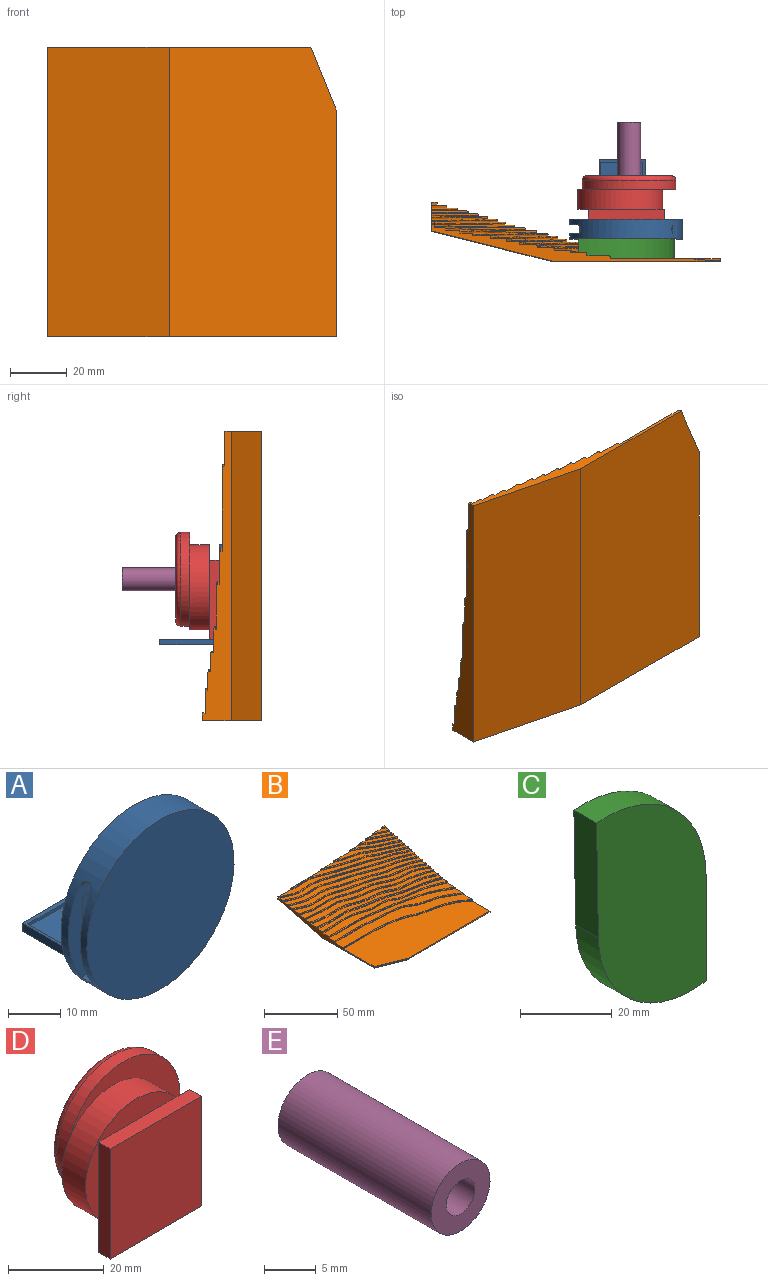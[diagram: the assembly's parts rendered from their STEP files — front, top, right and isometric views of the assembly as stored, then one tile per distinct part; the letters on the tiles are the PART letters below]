
ASSEMBLY  parts=5 mates=4
PART A: 31 faces, bbox 39.9x28x39.9 mm
  f0: plane 36.2x21.53mm, normal (0,-1,0), area 287.6mm2, adj f1,f14,f16,f17,f18,f19,f20,f21
  f1: cylinder r=19.96mm len=39.91mm, axis (0,-1,0), area 799mm2, adj f0,f3,f4,f14,f15,f16,f17
  f2: plane 21x16.52mm, normal (0,0,1), area 136.6mm2, adj f3,f5,f7,f8,f9,f10,f11,f12
  f3: plane 39.91x39.91mm, normal (0,1,0), area 1220mm2, adj f1,f2,f5,f6,f7
  f4: plane 39.91x39.91mm, normal (0,-1,0), area 1251mm2, adj f1
  f5: plane 21x1.88mm, normal (1,0,0), area 39.5mm2, adj f2,f3,f6,f8
  f6: plane 21x16.52mm, normal (0,0,-1), area 346.9mm2, adj f3,f5,f7,f8
  f7: plane 21x1.88mm, normal (-1,0,0), area 39.5mm2, adj f2,f3,f6,f8
  f8: plane 16.52x1.88mm, normal (0,1,0), area 31.1mm2, adj f2,f5,f6,f7
  f9: plane 14.58x0.7mm, normal (0,-1,0), area 10.2mm2, adj f2,f10,f12,f13
  f10: plane 14.42x0.7mm, normal (1,0,0), area 10.1mm2, adj f2,f9,f11,f13
  f11: plane 14.58x0.7mm, normal (0,1,0), area 10.2mm2, adj f2,f10,f12,f13
  f12: plane 14.42x0.7mm, normal (-1,0,0), area 10.1mm2, adj f2,f9,f11,f13
  f13: plane 14.58x14.42mm, normal (0,0,1), area 210.3mm2, adj f9,f10,f11,f12
  f14: cylinder r=1.62mm len=33.46mm, axis (1,0,0), area 166.7mm2, adj f0,f1,f15,f17
  f15: plane 36.2x21.53mm, normal (0,1,0), area 757.2mm2, adj f1,f14,f16,f17
  f16: plane 32.6x3.24mm, normal (0,0,1), area 105.5mm2, adj f0,f1,f15,f17
  f17: plane 23.02x3.24mm, normal (-1,0,0), area 73.7mm2, adj f0,f1,f14,f15,f16
  f18: plane 30.97x1.82mm, normal (0,0,-1), area 56.4mm2, adj f0,f19,f21,f22
  f19: plane 15.16x1.82mm, normal (1,0,0), area 27.6mm2, adj f0,f18,f20,f22
  f20: plane 30.97x1.82mm, normal (0,0,1), area 56.4mm2, adj f0,f19,f21,f22
  f21: plane 15.16x1.82mm, normal (-1,0,0), area 27.6mm2, adj f0,f18,f20,f22
  f22: plane 30.97x15.16mm, normal (0,-1,0), area 469.6mm2, adj f18,f19,f20,f21
  f23: cylinder r=17.46mm len=20.68mm, axis (0,-1,0), area 43.6mm2, adj f24,f25,f26
  f24: plane 20.68x3.39mm, normal (0,-1,0), area 47.7mm2, adj f23,f26
  f25: plane 20.56x3.35mm, normal (0,1,0), area 46.9mm2, adj f23,f26
  f26: cylinder r=4.12mm len=20.68mm, axis (1,0,0), area 41.2mm2, adj f23,f24,f25
  f27: plane 21.02x2mm, normal (0,0,-1), area 42mm2, adj f28,f29,f30
  f28: plane 21.02x3.52mm, normal (0,-1,0), area 50.4mm2, adj f27,f30
  f29: plane 21.02x3.52mm, normal (0,1,0), area 50.4mm2, adj f27,f30
  f30: cylinder r=17.46mm len=21.02mm, axis (0,-1,0), area 45.1mm2, adj f27,f28,f29
PART B: 75 faces, bbox 113.4x105.4x21.6 mm
  f0: plane 102.85x10.84mm, normal (0,1,0), area 515.5mm2, adj f1,f3,f29,f30,f31,f33,f34,f36
  f1: plane 93.19x13.13mm, normal (-1,0,0), area 217.1mm2, adj f0,f2,f5,f6,f7,f8,f9,f10
  f2: plane 102.21x59.09mm, normal (0,0,-1), area 5941.1mm2, adj f1,f3,f4,f48,f74
  f3: plane 102.21x21.2mm, normal (1,0,0), area 618.2mm2, adj f0,f2,f4,f5,f6,f7,f8,f9
  f4: plane 80.7x1.62mm, normal (0,-1,0), area 80mm2, adj f2,f3,f5,f48,f49
  f5: plane 102.21x39.62mm, normal (0,0,1), area 3289.8mm2, adj f1,f3,f4,f6,f49
  f6: extruded ~102.21x22.7mm, area 53.4mm2, adj f1,f3,f5,f72
  f7: plane 102.21x31.3mm, normal (0,0,1), area 884.1mm2, adj f1,f3,f8,f72
  f8: extruded ~102.21x21.85mm, area 53.2mm2, adj f1,f3,f7,f71
  f9: plane 102.21x26.47mm, normal (0,0,1), area 540.6mm2, adj f1,f3,f10,f71
  f10: extruded ~102.21x19.55mm, area 52.7mm2, adj f1,f3,f9,f70
  f11: plane 102.21x26.07mm, normal (0,0,1), area 497.7mm2, adj f1,f3,f12,f70
  f12: extruded ~102.21x18.81mm, area 52.7mm2, adj f1,f3,f11,f69
  f13: plane 102.21x22.91mm, normal (0,0,1), area 341.3mm2, adj f1,f3,f68,f69
  f14: plane 102.21x24.07mm, normal (0,0,1), area 313.2mm2, adj f1,f3,f66,f67
  f15: plane 102.21x25.31mm, normal (0,0,1), area 456.2mm2, adj f1,f3,f16,f17,f65
  f16: extruded ~29.65x1.56mm, area 14.9mm2, adj f1,f15,f17,f63
  f17: extruded ~72.56x19.99mm, area 37.9mm2, adj f3,f15,f16,f64
  f18: plane 102.21x26.36mm, normal (0,0,1), area 411.6mm2, adj f1,f3,f19,f63,f64
  f19: extruded ~102.21x23.57mm, area 53mm2, adj f1,f3,f18,f62
  f20: plane 102.21x29.38mm, normal (0,0,1), area 432.2mm2, adj f1,f3,f21,f62
  f21: extruded ~102.21x26.65mm, area 53.4mm2, adj f1,f3,f20,f61
  f22: plane 102.21x30.63mm, normal (0,0,1), area 382.6mm2, adj f1,f3,f23,f24,f61
  f23: extruded ~66.71x16.06mm, area 34.7mm2, adj f1,f22,f24,f60
  f24: extruded ~35.5x11.14mm, area 18.7mm2, adj f3,f22,f23,f73
  f25: plane 102.22x31.84mm, normal (0,0,1), area 409.8mm2, adj f1,f3,f26,f60,f73
  f26: extruded ~102.21x28.45mm, area 53.6mm2, adj f1,f3,f25,f59
  f27: plane 102.21x31.74mm, normal (0,0,1), area 331.8mm2, adj f1,f3,f28,f59
  f28: extruded ~102.21x28.42mm, area 53.5mm2, adj f1,f3,f27,f58
  f29: plane 102.21x29.28mm, normal (0,0,1), area 344.6mm2, adj f0,f1,f3,f30,f58
  f30: extruded ~90.49x26.05mm, area 47.6mm2, adj f0,f3,f29,f57
  f31: plane 89.45x25.54mm, normal (0,0,1), area 229.2mm2, adj f0,f3,f32,f33,f57
  f32: extruded ~17.29x7.32mm, area 9.4mm2, adj f3,f31,f33,f56
  f33: extruded ~43.55x15.97mm, area 23.3mm2, adj f0,f31,f32,f55
  f34: plane 59.47x22.74mm, normal (0,0,1), area 189.9mm2, adj f0,f3,f35,f36,f55,f56
  f35: extruded ~33.87x15.02mm, area 18.6mm2, adj f3,f34,f36,f53
  f36: extruded ~15.25x4.76mm, area 8mm2, adj f0,f34,f35,f54
  f37: plane 47.79x19.23mm, normal (0,0,1), area 148.4mm2, adj f0,f3,f38,f53,f54
  f38: extruded ~33.35x16.57mm, area 18.7mm2, adj f0,f3,f37,f52
  f39: plane 32.1x16.6mm, normal (0,0,1), area 91.9mm2, adj f0,f3,f40,f52
  f40: extruded ~24.46x12.88mm, area 13.9mm2, adj f0,f3,f39,f51
  f41: plane 23.6x12.33mm, normal (0,0,1), area 70.5mm2, adj f0,f3,f42,f51
  f42: extruded ~18.21x9.13mm, area 10.2mm2, adj f0,f3,f41,f50
  f43: plane 17.17x8.57mm, normal (0,0,1), area 45.2mm2, adj f0,f3,f44,f50
  f44: plane 11.3x5.41mm, normal (-0.43,-0.9,0), area 12.5mm2, adj f0,f3,f43,f45
  f45: plane 11.3x5.41mm, normal (0,0,1), area 27.8mm2, adj f0,f3,f44,f46
  f46: plane 2.76x2.02mm, normal (-0.59,-0.81,0), area 3.4mm2, adj f0,f3,f45,f47
  f47: plane 2.76x2.02mm, normal (0,0,1), area 2.8mm2, adj f0,f3,f46
  f48: plane 22.13x8.94mm, normal (-0.37,-0.93,0), area 11.9mm2, adj f1,f2,f4,f49
  f49: bspline ~26x10.89mm, area 20mm2, adj f1,f4,f5,f48
  f50: bspline ~20.24x10.5mm, area 16.1mm2, adj f0,f3,f42,f43
  f51: bspline ~26.81x14.55mm, area 22.1mm2, adj f0,f3,f40,f41
  f52: bspline ~37.03x18.43mm, area 29.5mm2, adj f0,f3,f38,f39
  f53: bspline ~35.79x16.28mm, area 30.1mm2, adj f3,f35,f37,f54
  f54: bspline ~16.1x5.52mm, area 12.5mm2, adj f0,f36,f37,f53
  f55: bspline ~46.35x17.45mm, area 37.2mm2, adj f0,f33,f34,f56
  f56: bspline ~18.36x8.18mm, area 15.1mm2, adj f3,f32,f34,f55
  f57: bspline ~95.26x28.48mm, area 76.6mm2, adj f0,f3,f30,f31
  f58: bspline ~110.14x31.71mm, area 86.9mm2, adj f1,f3,f28,f29
  f59: bspline ~112.34x33.81mm, area 88.5mm2, adj f1,f3,f26,f27
  f60: bspline ~70.67x18.2mm, area 56.4mm2, adj f1,f23,f25,f73
  f61: bspline ~109.5x30.43mm, area 87mm2, adj f1,f3,f21,f22
  f62: bspline ~112.46x28.05mm, area 85mm2, adj f1,f3,f19,f20
  f63: bspline ~32.8x2.26mm, area 24.2mm2, adj f1,f16,f18,f64
  f64: bspline ~79.82x23.26mm, area 60.8mm2, adj f3,f17,f18,f63
  f65: bspline ~109.59x24.96mm, area 85.7mm2, adj f1,f3,f15,f66
  f66: bspline ~110.15x25.16mm, area 85.1mm2, adj f1,f3,f14,f65
  f67: bspline ~110.29x21.38mm, area 85.3mm2, adj f1,f3,f14,f68
  f68: bspline ~110.14x21.42mm, area 85mm2, adj f1,f3,f13,f67
  f69: bspline ~112.54x21.38mm, area 84mm2, adj f1,f3,f12,f13
  f70: bspline ~112.4x22.72mm, area 85.4mm2, adj f1,f3,f10,f11
  f71: bspline ~112.44x25.14mm, area 86.6mm2, adj f1,f3,f8,f9
  f72: bspline ~111.97x26.59mm, area 86.3mm2, adj f1,f3,f6,f7
  f73: bspline ~37.07x12.24mm, area 29.2mm2, adj f3,f24,f25,f60
  f74: plane 102.21x42.91mm, normal (0,0.24,-0.97), area 4522.6mm2, adj f0,f1,f2,f3
PART C: 22 faces, bbox 33.8x7x59.6 mm
  f0: plane 31.01x7mm, normal (-1,0,-0.02), area 217.1mm2, adj f1,f3,f4,f5
  f1: cylinder r=28.97mm len=33.28mm, axis (0,1,0), area 345.2mm2, adj f0,f2,f4,f5
  f2: plane 28.12x7mm, normal (1,0,0), area 155.5mm2, adj f1,f3,f4,f5,f6,f7,f8,f9
  f3: cylinder r=31.13mm len=33.84mm, axis (0,1,0), area 361.3mm2, adj f0,f2,f4,f5
  f4: plane 59.57x33.84mm, normal (0,-1,0), area 1602.8mm2, adj f0,f1,f2,f3
  f5: plane 59.57x33.84mm, normal (0,1,0), area 1579.6mm2, adj f0,f1,f2,f3,f11
  f6: plane 16.8x9.2mm, normal (0,-1,0), area 131.4mm2, adj f2,f7,f9,f10,f11
  f7: cylinder r=1.73mm len=16.8mm, axis (1,0,0), area 91.4mm2, adj f2,f6,f8,f10
  f8: plane 16.8x9.2mm, normal (0,1,0), area 154.6mm2, adj f2,f7,f9,f10
  f9: cylinder r=1.73mm len=16.8mm, axis (1,0,0), area 91.4mm2, adj f2,f6,f8,f10
  f10: plane 12.67x3.46mm, normal (1,0,0), area 41.3mm2, adj f6,f7,f8,f9
  f11: cylinder r=2.72mm len=5.44mm, axis (0,-1,0), area 33.7mm2, adj f5,f6
  f12: plane 55.57x29.81mm, normal (0,1,0), area 1024.4mm2, adj f14,f15,f16,f17,f18,f19,f20,f21
  f13: plane 55.57x29.81mm, normal (0,-1,0), area 1030.5mm2, adj f14,f15,f16,f17,f18,f19,f20,f21
  f14: plane 5.08x3mm, normal (-1,0,0), area 14.3mm2, adj f12,f13,f16,f20
  f15: plane 29.08x3mm, normal (1,0,0.02), area 87.3mm2, adj f12,f13,f16,f18
  f16: cylinder r=26.97mm len=29.28mm, axis (0,1,0), area 132.6mm2, adj f12,f13,f14,f15
  f17: plane 5.42x3mm, normal (-1,0,0), area 15.4mm2, adj f12,f13,f18,f19
  f18: cylinder r=29.13mm len=29.81mm, axis (0,1,0), area 139.3mm2, adj f12,f13,f15,f17
  f19: cylinder r=3.73mm len=16.8mm, axis (1,0,0), area 52mm2, adj f12,f13,f17,f21
  f20: cylinder r=3.73mm len=16.8mm, axis (1,0,0), area 52mm2, adj f12,f13,f14,f21
  f21: plane 16.67x3mm, normal (-1,0,0), area 49.3mm2, adj f12,f13,f19,f20
PART D: 23 faces, bbox 36.2x15.4x39.3 mm
  f0: plane 28x3.5mm, normal (1,0,0), area 98mm2, adj f1,f3,f4,f5
  f1: plane 26.94x3.5mm, normal (0,0,-1), area 94.3mm2, adj f0,f2,f4,f5
  f2: plane 28.09x3.5mm, normal (-1,0,0), area 98.3mm2, adj f1,f3,f4,f5,f8
  f3: plane 26.94x3.5mm, normal (0,0,1), area 94.3mm2, adj f0,f2,f4,f5,f8
  f4: plane 28.09x26.94mm, normal (0,1,0), area 183.2mm2, adj f0,f1,f2,f3,f6
  f5: plane 28.09x26.94mm, normal (0,-1,0), area 755.4mm2, adj f0,f1,f2,f3
  f6: cylinder r=15.05mm len=30.1mm, axis (0,-1,0), area 661.9mm2, adj f4,f7,f8,f9
  f7: plane 23.69x22.31mm, normal (0,1,0), area 69.2mm2, adj f6,f10
  f8: plane 26.65x25mm, normal (0,-1,0), area 139.4mm2, adj f2,f3,f6
  f9: plane 32.62x32.1mm, normal (0,-1,0), area 219.6mm2, adj f6,f10
  f10: cylinder r=16.56mm len=33.13mm, axis (0,-1,0), area 327.8mm2, adj f7,f9,f12
  f11: plane 29.63x29.63mm, normal (0,1,0), area 136.2mm2, adj f12,f13
  f12: torus R=14.81mm, axis (0,1,0), area 275.1mm2, adj f10,f11
  f13: cylinder r=13.27mm len=26.54mm, axis (0,1,0), area 175.1mm2, adj f11,f14
  f14: plane 26.54x26.54mm, normal (0,1,0), area 553.3mm2, adj f13
  f15: cylinder r=13.05mm len=26.1mm, axis (0,-1,0), area 512.3mm2, adj f16,f17,f18,f19,f20,f21,f22
  f16: cylinder r=14.56mm len=19.38mm, axis (0,-1,0), area 87.2mm2, adj f15,f20,f22
  f17: plane 16.76x3.5mm, normal (1,0,0), area 58.6mm2, adj f15,f18,f19,f21
  f18: plane 19.9x3.5mm, normal (0,0,-1), area 69.7mm2, adj f15,f17,f19,f21
  f19: plane 22.34x20.64mm, normal (0,1,0), area 407.4mm2, adj f15,f17,f18
  f20: plane 20.75x19.57mm, normal (0,-1,0), area 60.4mm2, adj f15,f16
  f21: plane 23.67x22.22mm, normal (0,1,0), area 127.6mm2, adj f15,f17,f18
  f22: plane 24.74x24.41mm, normal (0,-1,0), area 474.7mm2, adj f15,f16
PART E: 4 faces, bbox 8.1x21x8.1 mm
  f0: cylinder r=1.98mm len=21mm, axis (0,-1,0), area 260.8mm2, adj f2,f3
  f1: cylinder r=4.04mm len=21mm, axis (0,-1,0), area 533mm2, adj f2,f3
  f2: plane 8.08x8.08mm, normal (0,1,0), area 39mm2, adj f0,f1
  f3: plane 8.08x8.08mm, normal (0,-1,0), area 39mm2, adj f0,f1
PLACE A t=(-49.15,-1.7,-14.41)mm
PLACE B rot(axis=(-0.58,0.58,0.58),120deg) t=(-83.01,-12,-17.74)mm
PLACE C t=(-48.45,-1,-15.74)mm
PLACE D t=(-45.22,-2.4,-14.5)mm
PLACE E t=(-45.28,-5.2,-22.77)mm
MATE fastened C.f4 <-> B.f5  axis (0,-1,0) through (-65.3,-11,-26.67)mm
MATE fastened E.f0 <-> D.f10  axis (0,-1,0) through (-64.33,16.3,-18.78)mm
MATE fastened D.f5 <-> A.f3  axis (0,-1,0) through (-65.37,3,-26.09)mm
MATE fastened A.f1 <-> C.f5  axis (0,-1,0) through (-65.4,-4,-26.46)mm
